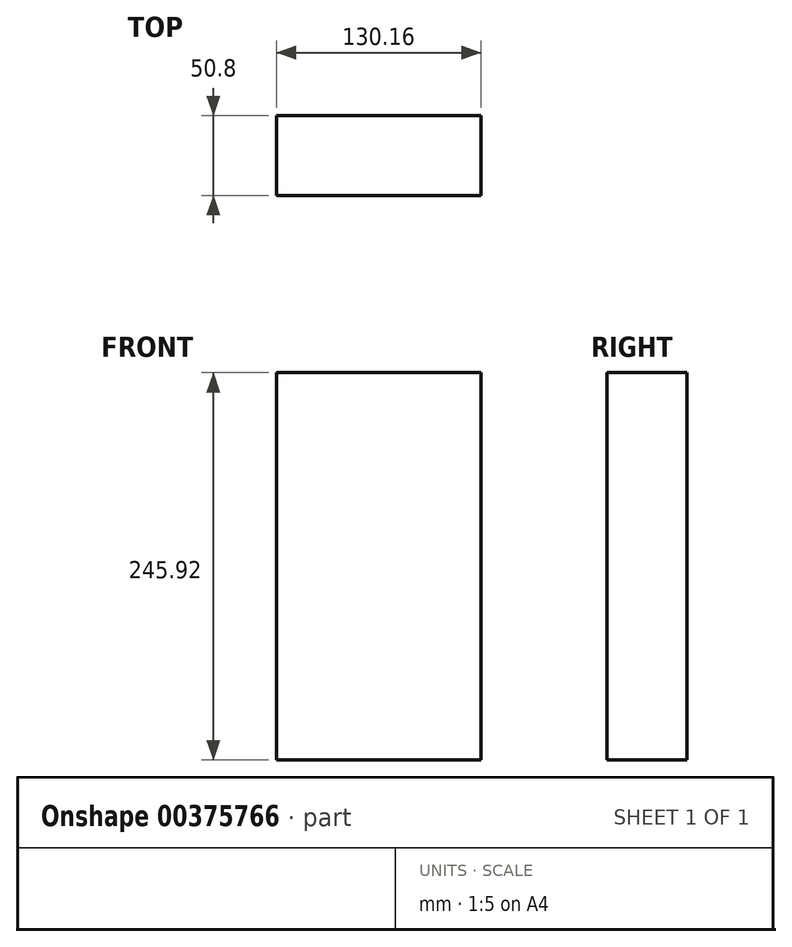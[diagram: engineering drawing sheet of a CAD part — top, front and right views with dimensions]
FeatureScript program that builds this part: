
annotation { "Feature Type Name" : "Feature", "Feature Type Description" : "" }
export const myFeature = defineFeature(function(context is Context, id is Id, definition is map)
    precondition{}
    {
        {
            var Q0;
            Q0=qCreatedBy(makeId("Front.planeOp"),FACE);
            var sketch = newSketch(context, id + "F0", { "sketchPlane" : qUnion([Q0])});
            skLineSegment(sketch, "E0.bottom", {"start": v(-65.08, -122.96) * mm, "end": v(65.08, -122.96) * mm});
            skLineSegment(sketch, "E0.top", {"start": v(-65.08, 122.96) * mm, "end": v(65.08, 122.96) * mm});
            skLineSegment(sketch, "E0.left", {"start": v(-65.08, -122.96) * mm, "end": v(-65.08, 122.96) * mm});
            skLineSegment(sketch, "E0.right", {"start": v(65.08, -122.96) * mm, "end": v(65.08, 122.96) * mm});
            skPoint(sketch, "E0.middle", {"position": v(0, 0) * mm});
            skPoint(sketch, "E1.middle", {"position": v(0, 76.65) * mm});
            skSolve(sketch);
        }
        {
            var Q0;
            Q0 = qSketchRegion(id + "F0", true);
            extrude(context, id + "F1", {"entities" : qUnion([Q0]), "depth" : 12.7 * mm, "hasSecondDirection" : true, "secondDirectionOppositeDirection" : true, "secondDirectionDepth" : 38.1 * mm});
        }
    });
